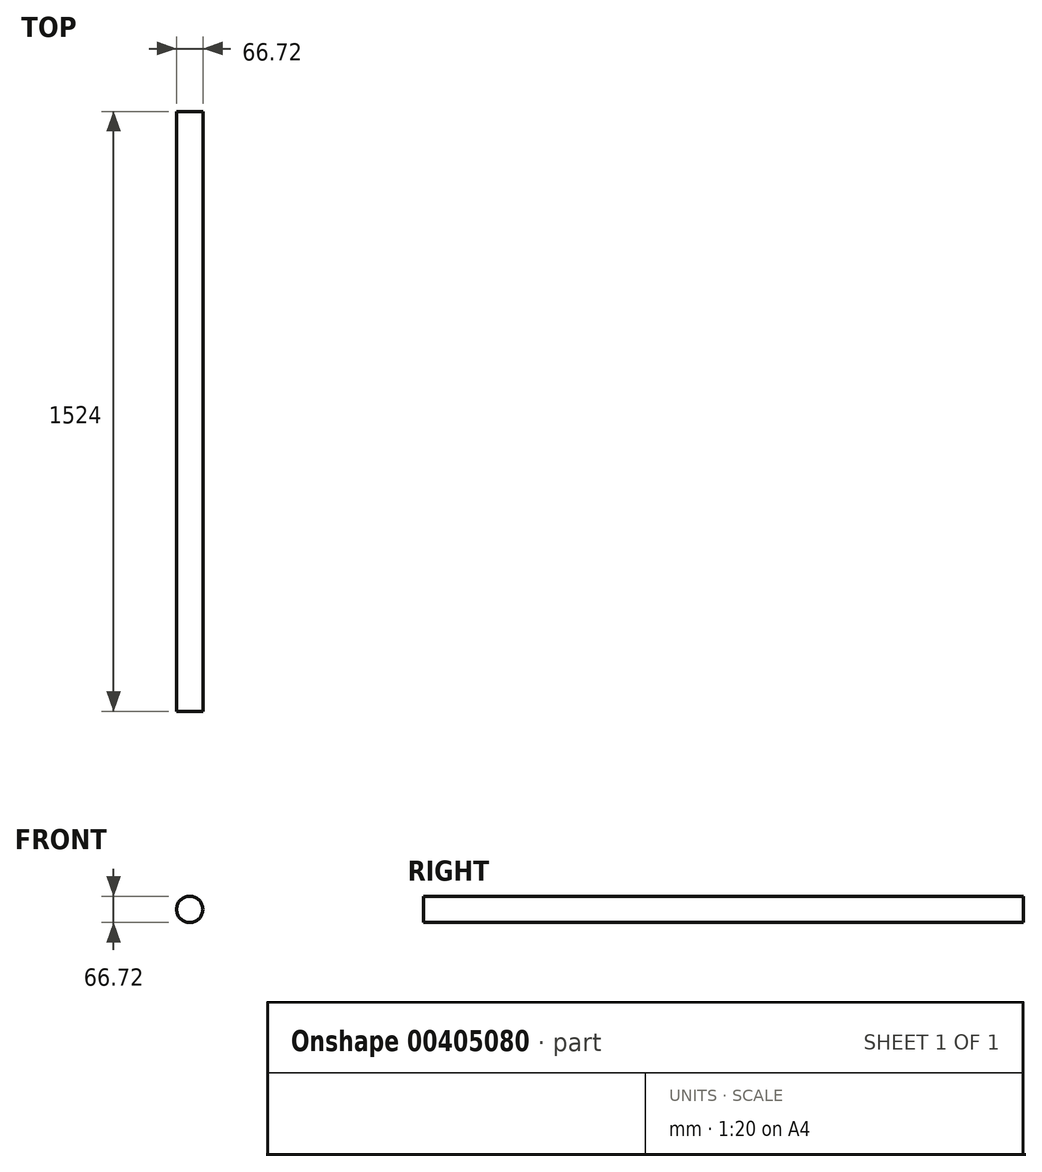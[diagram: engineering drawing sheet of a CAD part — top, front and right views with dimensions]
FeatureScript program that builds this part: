
annotation { "Feature Type Name" : "Feature", "Feature Type Description" : "" }
export const myFeature = defineFeature(function(context is Context, id is Id, definition is map)
    precondition{}
    {
        {
            var Q0;
            Q0=qCreatedBy(makeId("Front.planeOp"),FACE);
            var sketch = newSketch(context, id + "F0", { "sketchPlane" : qUnion([Q0])});
            skCircle(sketch, "E0", {"center": v(0, 92.37) * mm, "radius": 33.36 * mm});
            skSolve(sketch);
        }
        {
            var Q0;
            Q0 = qSketchRegion(id + "F0", true);
            extrude(context, id + "F1", {"entities" : qUnion([Q0]), "depth" : 1524 * mm});
        }
    });
